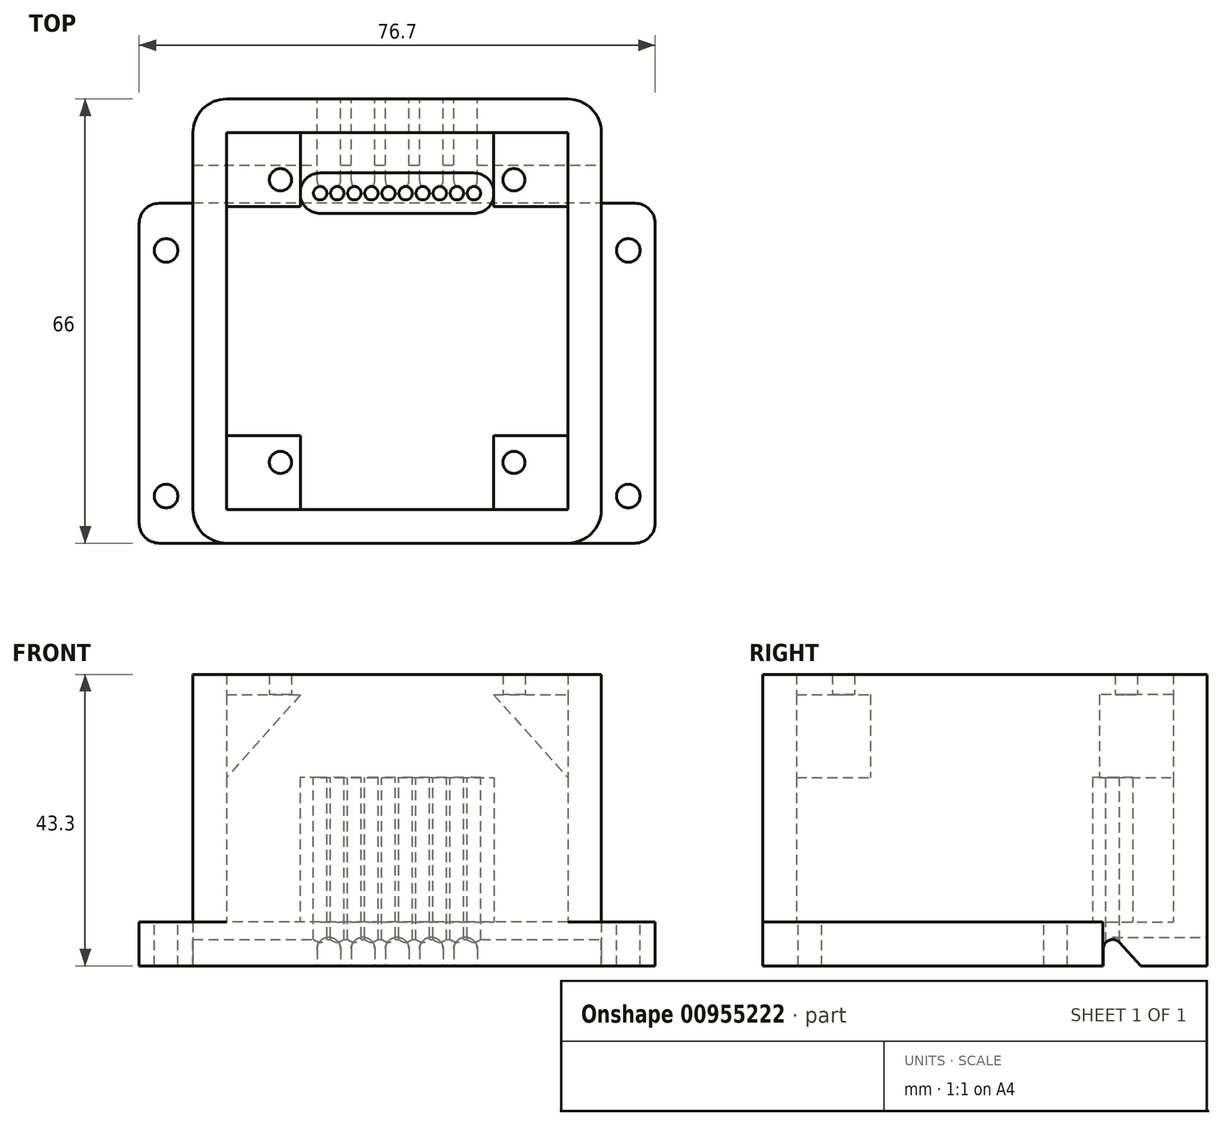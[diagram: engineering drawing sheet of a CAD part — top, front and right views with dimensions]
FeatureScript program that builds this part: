
annotation { "Feature Type Name" : "Feature", "Feature Type Description" : "" }
export const myFeature = defineFeature(function(context is Context, id is Id, definition is map)
    precondition{}
    {
        {
            var Q0;
            Q0=qCreatedBy(makeId("Top.planeOp"),FACE);
            var sketch = newSketch(context, id + "F0", { "sketchPlane" : qUnion([Q0])});
            skLineSegment(sketch, "E0.bottom", {"start": v(22.35, -25) * mm, "end": v(-22.35, -25) * mm});
            skLineSegment(sketch, "E0.top", {"start": v(22.35, 25) * mm, "end": v(-22.35, 25) * mm});
            skLineSegment(sketch, "E0.left", {"start": v(22.35, -25) * mm, "end": v(22.35, 25) * mm});
            skLineSegment(sketch, "E0.right", {"start": v(-22.35, -25) * mm, "end": v(-22.35, 25) * mm});
            skPoint(sketch, "E0.middle", {"position": v(0, 0) * mm});
            skSolve(sketch);
        }
        {
            var Q0;
            Q0=qCreatedBy(makeId("Top.planeOp"),FACE);
            var sketch = newSketch(context, id + "F1", { "sketchPlane" : qUnion([Q0])});
            skLineSegment(sketch, "E1.bottom", {"start": v(30.35, -33) * mm, "end": v(-30.35, -33) * mm});
            skLineSegment(sketch, "E1.top", {"start": v(25.35, 33) * mm, "end": v(-25.35, 33) * mm});
            skLineSegment(sketch, "E1.left", {"start": v(30.35, -33) * mm, "end": v(30.35, 28) * mm});
            skLineSegment(sketch, "E1.right", {"start": v(-30.35, -33) * mm, "end": v(-30.35, 28) * mm});
            skPoint(sketch, "E1.middle", {"position": v(0, 0) * mm});
            skPoint(sketch, "E2.visualSharp", {"position": v(-30.35, 33) * mm});
            skArc(sketch, "E2.filletArc", {"start": v(-25.35, 33) * mm, "mid": v(-28.89, 31.54) * mm, "end": v(-30.35, 28) * mm});
            skPoint(sketch, "E3.visualSharp", {"position": v(30.35, 33) * mm});
            skArc(sketch, "E3.filletArc", {"start": v(30.35, 28) * mm, "mid": v(28.89, 31.54) * mm, "end": v(25.35, 33) * mm});
            skPoint(sketch, "E4.visualSharp", {"position": v(-30.35, -33) * mm});
            skPoint(sketch, "E5.visualSharp", {"position": v(30.35, -33) * mm});
            skLineSegment(sketch, "E6", {"start": v(-20.48, 19) * mm, "end": v(20.95, 19) * mm, "construction": true});
            skLineSegment(sketch, "E7.bottom", {"start": v(-30.35, -33) * mm, "end": v(-35.35, -33) * mm});
            skLineSegment(sketch, "E7.top", {"start": v(-30.35, 17.5) * mm, "end": v(-35.35, 17.5) * mm});
            skLineSegment(sketch, "E7.left", {"start": v(-30.35, -33) * mm, "end": v(-30.35, 17.5) * mm});
            skLineSegment(sketch, "E7.right", {"start": v(-38.35, -30) * mm, "end": v(-38.35, 14.5) * mm});
            skPoint(sketch, "E8.oppositeSnap0", {"position": v(-34.35, 17.5) * mm});
            skLineSegment(sketch, "E8.bottom", {"start": v(30.35, -33) * mm, "end": v(35.35, -33) * mm});
            skLineSegment(sketch, "E8.top", {"start": v(30.35, 17.5) * mm, "end": v(35.35, 17.5) * mm});
            skLineSegment(sketch, "E8.left", {"start": v(30.35, -33) * mm, "end": v(30.35, 17.5) * mm});
            skLineSegment(sketch, "E8.right", {"start": v(38.35, -30) * mm, "end": v(38.35, 14.5) * mm});
            skPoint(sketch, "E9.visualSharp", {"position": v(-38.35, 17.5) * mm});
            skArc(sketch, "E9.filletArc", {"start": v(-35.35, 17.5) * mm, "mid": v(-37.47, 16.62) * mm, "end": v(-38.35, 14.5) * mm});
            skPoint(sketch, "E10.visualSharp", {"position": v(-38.35, -33) * mm});
            skArc(sketch, "E10.filletArc", {"start": v(-38.35, -30) * mm, "mid": v(-37.47, -32.12) * mm, "end": v(-35.35, -33) * mm});
            skPoint(sketch, "E11.visualSharp", {"position": v(38.35, 17.5) * mm});
            skArc(sketch, "E11.filletArc", {"start": v(38.35, 14.5) * mm, "mid": v(37.47, 16.62) * mm, "end": v(35.35, 17.5) * mm});
            skPoint(sketch, "E12.visualSharp", {"position": v(38.35, -33) * mm});
            skArc(sketch, "E12.filletArc", {"start": v(35.35, -33) * mm, "mid": v(37.47, -32.12) * mm, "end": v(38.35, -30) * mm});
            skSolve(sketch);
        }
        {
            var Q0;
            Q0=makeQuery(id+"F1.imprint","IMPRINT",FACE,{"disambiguationData":[TD([[makeQuery(id+"F1.imprint","IMPRINT",EDGE,{"derivedFrom":sQuery(id+"F1.wireOp",EDGE,"E1.bottom")}),-1.0]])]});
            var Q1;
            Q1=makeQuery(id+"F1.imprint","IMPRINT",FACE,{"disambiguationData":[TD([[makeQuery(id+"F1.imprint","IMPRINT",EDGE,{"derivedFrom":sQuery(id+"F1.wireOp",EDGE,"E7.bottom")}),-1.0]])]});
            var Q2;
            Q2=makeQuery(id+"F1.imprint","IMPRINT",FACE,{"disambiguationData":[TD([[makeQuery(id+"F1.imprint","IMPRINT",EDGE,{"derivedFrom":sQuery(id+"F1.wireOp",EDGE,"E8.bottom")}),1.0]])]});
            extrude(context, id + "F2", {"entities" : qUnion([Q0, Q1, Q2]), "depth" : 6.5 * mm, "offsetDistance" : 25 * mm});
        }
        {
            var Q0;
            Q0=makeQuery(id+"F2.opExtrude","CAP_FACE",FACE,{"disambiguationData":[OSD([sQuery(id+"F1.wireOp",EDGE,"E1.bottom"),sQuery(id+"F1.wireOp",EDGE,"E1.top"),sQuery(id+"F1.wireOp",EDGE,"E1.left"),sQuery(id+"F1.wireOp",EDGE,"E1.right"),sQuery(id+"F1.wireOp",EDGE,"E2.filletArc"),sQuery(id+"F1.wireOp",EDGE,"E3.filletArc"),sQuery(id+"F1.wireOp",EDGE,"E4.filletArc"),sQuery(id+"F1.wireOp",EDGE,"E5.filletArc")])],"isStart":false});
            var sketch = newSketch(context, id + "F3", { "sketchPlane" : qUnion([Q0])});
            skLineSegment(sketch, "E13.bottom", {"start": v(25.35, -28) * mm, "end": v(-25.35, -28) * mm});
            skLineSegment(sketch, "E13.top", {"start": v(25.35, 28) * mm, "end": v(-25.35, 28) * mm});
            skLineSegment(sketch, "E13.left", {"start": v(25.35, -28) * mm, "end": v(25.35, 28) * mm});
            skLineSegment(sketch, "E13.right", {"start": v(-25.35, -28) * mm, "end": v(-25.35, 28) * mm});
            skPoint(sketch, "E13.middle", {"position": v(0, 0) * mm});
            skLineSegment(sketch, "E14.bottom", {"start": v(-15.24, 28) * mm, "end": v(15.24, 28) * mm});
            skLineSegment(sketch, "E14.top", {"start": v(-11.45, 16) * mm, "end": v(11.4, 16) * mm});
            skPoint(sketch, "E15", {"position": v(-11.45, 19) * mm});
            skPoint(sketch, "E16", {"position": v(-8.91, 19) * mm});
            skPoint(sketch, "E17", {"position": v(-6.37, 19) * mm});
            skPoint(sketch, "E18", {"position": v(-3.83, 19) * mm});
            skPoint(sketch, "E19", {"position": v(-1.3, 19) * mm});
            skPoint(sketch, "E20", {"position": v(1.25, 19) * mm});
            skPoint(sketch, "E21", {"position": v(3.79, 19) * mm});
            skPoint(sketch, "E22", {"position": v(6.33, 19) * mm});
            skPoint(sketch, "E23", {"position": v(8.87, 19) * mm});
            skPoint(sketch, "E24", {"position": v(11.4, 19) * mm});
            skPoint(sketch, "E25.visualSharp", {"position": v(15.24, 16) * mm});
            skLineSegment(sketch, "E26.top", {"start": v(-11.45, 22) * mm, "end": v(11.4, 22) * mm});
            skArc(sketch, "E27", {"start": v(-11.45, 22) * mm, "mid": v(-14.45, 19) * mm, "end": v(-11.45, 16) * mm});
            skArc(sketch, "E28", {"start": v(11.4, 16) * mm, "mid": v(14.4, 19) * mm, "end": v(11.4, 22) * mm});
            skLineSegment(sketch, "E29.bottom", {"start": v(25.35, -33) * mm, "end": v(-25.35, -33) * mm});
            skLineSegment(sketch, "E29.top", {"start": v(25.35, 33) * mm, "end": v(-25.35, 33) * mm});
            skLineSegment(sketch, "E29.left", {"start": v(30.35, -28) * mm, "end": v(30.35, 28) * mm});
            skLineSegment(sketch, "E29.right", {"start": v(-30.35, -28) * mm, "end": v(-30.35, 28) * mm});
            skPoint(sketch, "E30.visualSharp", {"position": v(-30.35, -33) * mm});
            skArc(sketch, "E30.filletArc", {"start": v(-30.35, -28) * mm, "mid": v(-28.89, -31.54) * mm, "end": v(-25.35, -33) * mm});
            skPoint(sketch, "E31.visualSharp", {"position": v(30.35, -33) * mm});
            skArc(sketch, "E31.filletArc", {"start": v(25.35, -33) * mm, "mid": v(28.89, -31.54) * mm, "end": v(30.35, -28) * mm});
            skPoint(sketch, "E32.visualSharp", {"position": v(-30.35, 33) * mm});
            skArc(sketch, "E32.filletArc", {"start": v(-25.35, 33) * mm, "mid": v(-28.89, 31.54) * mm, "end": v(-30.35, 28) * mm});
            skPoint(sketch, "E33.visualSharp", {"position": v(30.35, 33) * mm});
            skArc(sketch, "E33.filletArc", {"start": v(30.35, 28) * mm, "mid": v(28.89, 31.54) * mm, "end": v(25.35, 33) * mm});
            skSolve(sketch);
        }
        {
            var Q0;
            Q0=makeQuery(id+"F3.imprint","IMPRINT",FACE,{"disambiguationData":[TD([[makeQuery(id+"F3.imprint","IMPRINT",EDGE,{"derivedFrom":sQuery(id+"F3.wireOp",EDGE,"E13.bottom")}),1.0]])]});
            var Q1;
            Q1=makeQuery(id+"F3.imprint","IMPRINT",FACE,{"disambiguationData":[TD([[makeQuery(id+"F3.imprint","IMPRINT",EDGE,{"derivedFrom":sQuery(id+"F3.wireOp",EDGE,"E14.top")}),1.0]])]});
            extrude(context, id + "F4", {"entities" : qUnion([Q0, Q1]), "operationType" : NewBodyOperationType.ADD, "depth" : 21.5 * mm, "offsetDistance" : 25 * mm});
        }
        {
            var Q0;
            {var subQ0=sQuery(id+"F1.wireOp",EDGE,"E1.left");Q0=makeQuery(id+"F4.boolean.opBoolean","MERGE",FACE,{"derivedFrom":[makeQuery(id+"F2.opExtrude","SWEPT_FACE",FACE,{"disambiguationData":[OSD([subQ0])]}),makeQuery(id+"F4.opExtrude","SWEPT_FACE",FACE,{"disambiguationData":[OSD([subQ0])]})]});}
            var sketch = newSketch(context, id + "F5", { "sketchPlane" : qUnion([Q0])});
            skLineSegment(sketch, "E34", {"start": v(19, 18.6) * mm, "end": v(19, -3.34) * mm, "construction": true});
            skPoint(sketch, "E35", {"position": v(19, 2.5) * mm});
            skCircle(sketch, "E36", {"center": v(19, 2.5) * mm, "radius": 1.4 * mm});
            skLineSegment(sketch, "E37", {"start": v(17.6, 2.5) * mm, "end": v(17.6, 0) * mm});
            skLineSegment(sketch, "E38", {"start": v(23.2, 0) * mm, "end": v(20.03, 3.45) * mm});
            skSolve(sketch);
        }
        {
            var Q0;
            {var subQ0=sQuery(id+"F5.wireOp",EDGE,"E36");var subQ1=makeQuery(id+"F5.imprint","INTERSECT",VERTEX,{"derivedFrom":[subQ0,sQuery(id+"F5.wireOp",EDGE,"E37")]});Q0=makeQuery(id+"F5.imprint","IMPRINT",FACE,{"disambiguationData":[TD([[makeQuery(id+"F5.imprint","IMPRINT",EDGE,{"disambiguationData":[TD([[subQ1,1.0]])],"derivedFrom":subQ0}),1.0]])]});}
            var Q1;
            {var subQ0=sQuery(id+"F5.wireOp",EDGE,"E37");Q1=makeQuery(id+"F5.imprint","IMPRINT",FACE,{"disambiguationData":[TD([[makeQuery(id+"F5.imprint","IMPRINT",EDGE,{"derivedFrom":subQ0}),1.0]])]});}
            extrude(context, id + "F6", {"entities" : qUnion([Q0, Q1]), "operationType" : NewBodyOperationType.REMOVE, "endBound" : BoundingType.THROUGH_ALL, "oppositeDirection" : true, "depth" : 25 * mm, "offsetDistance" : 25 * mm});
        }
        {
            var Q0;
            Q0=makeQuery(id+"F4.opExtrude","CAP_FACE",FACE,{"disambiguationData":[OSD([sQuery(id+"F3.wireOp",EDGE,"E13.bottom"),sQuery(id+"F3.wireOp",EDGE,"E13.top"),sQuery(id+"F3.wireOp",EDGE,"E13.left"),sQuery(id+"F3.wireOp",EDGE,"E13.right"),sQuery(id+"F3.wireOp",EDGE,"E29.bottom"),sQuery(id+"F3.wireOp",EDGE,"E29.top"),sQuery(id+"F3.wireOp",EDGE,"E29.left"),sQuery(id+"F3.wireOp",EDGE,"E29.right"),sQuery(id+"F3.wireOp",EDGE,"E30.filletArc"),sQuery(id+"F3.wireOp",EDGE,"E31.filletArc"),sQuery(id+"F3.wireOp",EDGE,"E32.filletArc"),sQuery(id+"F3.wireOp",EDGE,"E33.filletArc")])],"isStart":false});
            var sketch = newSketch(context, id + "F7", { "sketchPlane" : qUnion([Q0])});
            skPoint(sketch, "E39", {"position": v(-11.45, 19) * mm});
            skCircle(sketch, "E40", {"center": v(-11.45, 19) * mm, "radius": 1 * mm});
            skPoint(sketch, "E41", {"position": v(-8.91, 19) * mm});
            skPoint(sketch, "E42", {"position": v(-6.37, 19) * mm});
            skPoint(sketch, "E43", {"position": v(-3.83, 19) * mm});
            skPoint(sketch, "E44", {"position": v(-1.3, 19) * mm});
            skPoint(sketch, "E45", {"position": v(1.25, 19) * mm});
            skPoint(sketch, "E46", {"position": v(3.79, 19) * mm});
            skPoint(sketch, "E47", {"position": v(6.33, 19) * mm});
            skPoint(sketch, "E48", {"position": v(8.87, 19) * mm});
            skPoint(sketch, "E49", {"position": v(11.4, 19) * mm});
            skCircle(sketch, "E50", {"center": v(-8.91, 19) * mm, "radius": 1 * mm});
            skCircle(sketch, "E51", {"center": v(-6.37, 19) * mm, "radius": 1 * mm});
            skCircle(sketch, "E52", {"center": v(-3.83, 19) * mm, "radius": 1 * mm});
            skCircle(sketch, "E53", {"center": v(-1.3, 19) * mm, "radius": 1 * mm});
            skCircle(sketch, "E54", {"center": v(1.25, 19) * mm, "radius": 1 * mm});
            skCircle(sketch, "E55", {"center": v(3.79, 19) * mm, "radius": 1 * mm});
            skCircle(sketch, "E56", {"center": v(6.33, 19) * mm, "radius": 1 * mm});
            skCircle(sketch, "E57", {"center": v(8.87, 19) * mm, "radius": 1 * mm});
            skCircle(sketch, "E58", {"center": v(11.4, 19) * mm, "radius": 1 * mm});
            skSolve(sketch);
        }
        {
            var Q0;
            Q0=makeQuery(id+"F7.imprint","IMPRINT",FACE,{"disambiguationData":[TD([[makeQuery(id+"F7.imprint","IMPRINT",EDGE,{"derivedFrom":sQuery(id+"F7.wireOp",EDGE,"E53")}),1.0]])]});
            var Q1;
            Q1=makeQuery(id+"F7.imprint","IMPRINT",FACE,{"disambiguationData":[TD([[makeQuery(id+"F7.imprint","IMPRINT",EDGE,{"derivedFrom":sQuery(id+"F7.wireOp",EDGE,"E40")}),1.0]])]});
            var Q2;
            Q2=makeQuery(id+"F7.imprint","IMPRINT",FACE,{"disambiguationData":[TD([[makeQuery(id+"F7.imprint","IMPRINT",EDGE,{"derivedFrom":sQuery(id+"F7.wireOp",EDGE,"E50")}),1.0]])]});
            var Q3;
            Q3=makeQuery(id+"F7.imprint","IMPRINT",FACE,{"disambiguationData":[TD([[makeQuery(id+"F7.imprint","IMPRINT",EDGE,{"derivedFrom":sQuery(id+"F7.wireOp",EDGE,"E51")}),1.0]])]});
            var Q4;
            Q4=makeQuery(id+"F7.imprint","IMPRINT",FACE,{"disambiguationData":[TD([[makeQuery(id+"F7.imprint","IMPRINT",EDGE,{"derivedFrom":sQuery(id+"F7.wireOp",EDGE,"E52")}),1.0]])]});
            var Q5;
            Q5=makeQuery(id+"F7.imprint","IMPRINT",FACE,{"disambiguationData":[TD([[makeQuery(id+"F7.imprint","IMPRINT",EDGE,{"derivedFrom":sQuery(id+"F7.wireOp",EDGE,"E54")}),1.0]])]});
            var Q6;
            Q6=makeQuery(id+"F7.imprint","IMPRINT",FACE,{"disambiguationData":[TD([[makeQuery(id+"F7.imprint","IMPRINT",EDGE,{"derivedFrom":sQuery(id+"F7.wireOp",EDGE,"E55")}),1.0]])]});
            var Q7;
            Q7=makeQuery(id+"F7.imprint","IMPRINT",FACE,{"disambiguationData":[TD([[makeQuery(id+"F7.imprint","IMPRINT",EDGE,{"derivedFrom":sQuery(id+"F7.wireOp",EDGE,"E56")}),1.0]])]});
            var Q8;
            Q8=makeQuery(id+"F7.imprint","IMPRINT",FACE,{"disambiguationData":[TD([[makeQuery(id+"F7.imprint","IMPRINT",EDGE,{"derivedFrom":sQuery(id+"F7.wireOp",EDGE,"E57")}),1.0]])]});
            var Q9;
            Q9=makeQuery(id+"F7.imprint","IMPRINT",FACE,{"disambiguationData":[TD([[makeQuery(id+"F7.imprint","IMPRINT",EDGE,{"derivedFrom":sQuery(id+"F7.wireOp",EDGE,"E58")}),1.0]])]});
            extrude(context, id + "F8", {"entities" : qUnion([Q0, Q1, Q2, Q3, Q4, Q5, Q6, Q7, Q8, Q9]), "operationType" : NewBodyOperationType.REMOVE, "oppositeDirection" : true, "depth" : 26 * mm, "offsetDistance" : 25 * mm});
        }
        {
            var Q0;
            Q0=makeQuery(id+"F4.opExtrude","CAP_FACE",FACE,{"disambiguationData":[OSD([sQuery(id+"F3.wireOp",EDGE,"E13.bottom"),sQuery(id+"F3.wireOp",EDGE,"E13.top"),sQuery(id+"F3.wireOp",EDGE,"E13.left"),sQuery(id+"F3.wireOp",EDGE,"E13.right"),sQuery(id+"F3.wireOp",EDGE,"E29.bottom"),sQuery(id+"F3.wireOp",EDGE,"E29.top"),sQuery(id+"F3.wireOp",EDGE,"E29.left"),sQuery(id+"F3.wireOp",EDGE,"E29.right"),sQuery(id+"F3.wireOp",EDGE,"E30.filletArc"),sQuery(id+"F3.wireOp",EDGE,"E31.filletArc"),sQuery(id+"F3.wireOp",EDGE,"E32.filletArc"),sQuery(id+"F3.wireOp",EDGE,"E33.filletArc")])],"isStart":false});
            var sketch = newSketch(context, id + "F9", { "sketchPlane" : qUnion([Q0])});
            skLineSegment(sketch, "E59.bottom", {"start": v(-25.35, 28) * mm, "end": v(-14.35, 28) * mm});
            skLineSegment(sketch, "E59.top", {"start": v(-25.35, 17) * mm, "end": v(-14.35, 17) * mm});
            skLineSegment(sketch, "E59.left", {"start": v(-25.35, 28) * mm, "end": v(-25.35, 17) * mm});
            skLineSegment(sketch, "E59.right", {"start": v(-14.35, 28) * mm, "end": v(-14.35, 17) * mm});
            skLineSegment(sketch, "E60.bottom", {"start": v(25.35, 28) * mm, "end": v(14.35, 28) * mm});
            skLineSegment(sketch, "E60.top", {"start": v(25.35, 17) * mm, "end": v(14.35, 17) * mm});
            skLineSegment(sketch, "E60.left", {"start": v(25.35, 28) * mm, "end": v(25.35, 17) * mm});
            skLineSegment(sketch, "E60.right", {"start": v(14.35, 28) * mm, "end": v(14.35, 17) * mm});
            skLineSegment(sketch, "E61.bottom", {"start": v(-25.35, -28) * mm, "end": v(-14.35, -28) * mm});
            skLineSegment(sketch, "E61.top", {"start": v(-25.35, -17) * mm, "end": v(-14.35, -17) * mm});
            skLineSegment(sketch, "E61.left", {"start": v(-25.35, -28) * mm, "end": v(-25.35, -17) * mm});
            skLineSegment(sketch, "E61.right", {"start": v(-14.35, -28) * mm, "end": v(-14.35, -17) * mm});
            skLineSegment(sketch, "E62.bottom", {"start": v(25.35, -28) * mm, "end": v(14.35, -28) * mm});
            skLineSegment(sketch, "E62.top", {"start": v(25.35, -17) * mm, "end": v(14.35, -17) * mm});
            skLineSegment(sketch, "E62.left", {"start": v(25.35, -28) * mm, "end": v(25.35, -17) * mm});
            skLineSegment(sketch, "E62.right", {"start": v(14.35, -28) * mm, "end": v(14.35, -17) * mm});
            skSolve(sketch);
        }
        {
            var Q0;
            {var subQ5=sQuery(id+"F9.wireOp",EDGE,"E59.bottom");Q0=makeQuery(id+"F9.imprint","IMPRINT",FACE,{"disambiguationData":[TD([[makeQuery(id+"F9.imprint","IMPRINT",EDGE,{"derivedFrom":subQ5}),-1.0]])]});}
            var Q1;
            Q1=makeQuery(id+"F9.imprint","IMPRINT",FACE,{"disambiguationData":[TD([[makeQuery(id+"F9.imprint","IMPRINT",EDGE,{"derivedFrom":sQuery(id+"F9.wireOp",EDGE,"E59.bottom")}),1.0]])]});
            var Q2;
            Q2=makeQuery(id+"F9.imprint","IMPRINT",FACE,{"disambiguationData":[TD([[makeQuery(id+"F9.imprint","IMPRINT",EDGE,{"derivedFrom":sQuery(id+"F9.wireOp",EDGE,"E60.bottom")}),1.0]])]});
            var Q3;
            Q3=makeQuery(id+"F9.imprint","IMPRINT",FACE,{"disambiguationData":[TD([[makeQuery(id+"F9.imprint","IMPRINT",EDGE,{"derivedFrom":sQuery(id+"F9.wireOp",EDGE,"E61.bottom")}),-1.0]])]});
            var Q4;
            Q4=makeQuery(id+"F9.imprint","IMPRINT",FACE,{"disambiguationData":[TD([[makeQuery(id+"F9.imprint","IMPRINT",EDGE,{"derivedFrom":sQuery(id+"F9.wireOp",EDGE,"E62.bottom")}),-1.0]])]});
            extrude(context, id + "F10", {"entities" : qUnion([Q0, Q1, Q2, Q3, Q4]), "operationType" : NewBodyOperationType.ADD, "depth" : 12.3 * mm, "offsetDistance" : 25 * mm});
        }
        {
            var Q0;
            Q0=makeQuery(id+"F10.opExtrude","SWEPT_FACE",FACE,{"disambiguationData":[OSD([sQuery(id+"F9.wireOp",EDGE,"E59.top")])]});
            var sketch = newSketch(context, id + "F11", { "sketchPlane" : qUnion([Q0])});
            skLineSegment(sketch, "E63", {"start": v(-14.35, 40.3) * mm, "end": v(-25.35, 28) * mm});
            skLineSegment(sketch, "E64", {"start": v(-25.35, 28) * mm, "end": v(-14.35, 28) * mm});
            skLineSegment(sketch, "E65", {"start": v(-14.35, 28) * mm, "end": v(-14.35, 40.3) * mm});
            skSolve(sketch);
        }
        {
            var Q0;
            {var subQ0=sQuery(id+"F11.wireOp",EDGE,"E63");Q0=makeQuery(id+"F11.imprint","IMPRINT",FACE,{"disambiguationData":[TD([[makeQuery(id+"F11.imprint","IMPRINT",EDGE,{"derivedFrom":subQ0}),1.0]])]});}
            extrude(context, id + "F12", {"entities" : qUnion([Q0]), "operationType" : NewBodyOperationType.REMOVE, "oppositeDirection" : true, "depth" : 11 * mm, "offsetDistance" : 25 * mm});
        }
        {
            var Q0;
            Q0=makeQuery(id+"F10.opExtrude","SWEPT_FACE",FACE,{"disambiguationData":[OSD([sQuery(id+"F9.wireOp",EDGE,"E60.top")])]});
            var sketch = newSketch(context, id + "F13", { "sketchPlane" : qUnion([Q0])});
            skLineSegment(sketch, "E66", {"start": v(14.35, 40.3) * mm, "end": v(25.35, 28) * mm});
            skLineSegment(sketch, "E67", {"start": v(25.35, 28) * mm, "end": v(14.35, 28) * mm});
            skLineSegment(sketch, "E68", {"start": v(14.35, 28) * mm, "end": v(14.35, 40.3) * mm});
            skSolve(sketch);
        }
        {
            var Q0;
            {var subQ0=sQuery(id+"F13.wireOp",EDGE,"E66");Q0=makeQuery(id+"F13.imprint","IMPRINT",FACE,{"disambiguationData":[TD([[makeQuery(id+"F13.imprint","IMPRINT",EDGE,{"derivedFrom":subQ0}),-1.0]])]});}
            extrude(context, id + "F14", {"entities" : qUnion([Q0]), "operationType" : NewBodyOperationType.REMOVE, "oppositeDirection" : true, "depth" : 11 * mm, "offsetDistance" : 25 * mm});
        }
        {
            var Q0;
            Q0=makeQuery(id+"F10.opExtrude","SWEPT_FACE",FACE,{"disambiguationData":[OSD([sQuery(id+"F9.wireOp",EDGE,"E62.top")])]});
            var sketch = newSketch(context, id + "F15", { "sketchPlane" : qUnion([Q0])});
            skLineSegment(sketch, "E69", {"start": v(-25.35, 28) * mm, "end": v(-14.35, 40.3) * mm});
            skLineSegment(sketch, "E70", {"start": v(-14.35, 40.3) * mm, "end": v(-14.35, 28) * mm});
            skLineSegment(sketch, "E71", {"start": v(-14.35, 28) * mm, "end": v(-25.35, 28) * mm});
            skSolve(sketch);
        }
        {
            var Q0;
            Q0=makeQuery(id+"F15.imprint","IMPRINT",FACE,{"disambiguationData":[TD([[makeQuery(id+"F15.imprint","IMPRINT",EDGE,{"derivedFrom":sQuery(id+"F15.wireOp",EDGE,"E69")}),-1.0]])]});
            extrude(context, id + "F16", {"entities" : qUnion([Q0]), "operationType" : NewBodyOperationType.REMOVE, "oppositeDirection" : true, "depth" : 11 * mm, "offsetDistance" : 25 * mm});
        }
        {
            var Q0;
            Q0=makeQuery(id+"F10.opExtrude","SWEPT_FACE",FACE,{"disambiguationData":[OSD([sQuery(id+"F9.wireOp",EDGE,"E61.top")])]});
            var sketch = newSketch(context, id + "F17", { "sketchPlane" : qUnion([Q0])});
            skLineSegment(sketch, "E72", {"start": v(14.35, 40.3) * mm, "end": v(25.35, 28) * mm});
            skLineSegment(sketch, "E73", {"start": v(25.35, 28) * mm, "end": v(14.35, 28) * mm});
            skLineSegment(sketch, "E74", {"start": v(14.35, 28) * mm, "end": v(14.35, 40.3) * mm});
            skSolve(sketch);
        }
        {
            var Q0;
            Q0=makeQuery(id+"F17.imprint","IMPRINT",FACE,{"disambiguationData":[TD([[makeQuery(id+"F17.imprint","IMPRINT",EDGE,{"derivedFrom":sQuery(id+"F17.wireOp",EDGE,"E72")}),-1.0]])]});
            extrude(context, id + "F18", {"entities" : qUnion([Q0]), "operationType" : NewBodyOperationType.REMOVE, "oppositeDirection" : true, "depth" : 11 * mm, "offsetDistance" : 25 * mm});
        }
        {
            var Q0;
            Q0=makeQuery(id+"F10.opExtrude","CAP_FACE",FACE,{"disambiguationData":[OSD([sQuery(id+"F3.wireOp",EDGE,"E13.bottom"),sQuery(id+"F3.wireOp",EDGE,"E13.top"),sQuery(id+"F3.wireOp",EDGE,"E13.left"),sQuery(id+"F3.wireOp",EDGE,"E13.right"),sQuery(id+"F3.wireOp",EDGE,"E29.bottom"),sQuery(id+"F3.wireOp",EDGE,"E29.top"),sQuery(id+"F3.wireOp",EDGE,"E29.left"),sQuery(id+"F3.wireOp",EDGE,"E29.right"),sQuery(id+"F3.wireOp",EDGE,"E30.filletArc"),sQuery(id+"F3.wireOp",EDGE,"E31.filletArc"),sQuery(id+"F3.wireOp",EDGE,"E32.filletArc"),sQuery(id+"F3.wireOp",EDGE,"E33.filletArc"),sQuery(id+"F9.wireOp",EDGE,"E59.top"),sQuery(id+"F9.wireOp",EDGE,"E59.right"),sQuery(id+"F9.wireOp",EDGE,"E60.top"),sQuery(id+"F9.wireOp",EDGE,"E60.right"),sQuery(id+"F9.wireOp",EDGE,"E61.top"),sQuery(id+"F9.wireOp",EDGE,"E61.right"),sQuery(id+"F9.wireOp",EDGE,"E62.top"),sQuery(id+"F9.wireOp",EDGE,"E62.right")])],"isStart":false});
            var sketch = newSketch(context, id + "F19", { "sketchPlane" : qUnion([Q0])});
            skPoint(sketch, "E75", {"position": v(-17.35, 21) * mm});
            skPoint(sketch, "E76", {"position": v(17.35, 21) * mm});
            skCircle(sketch, "E77", {"center": v(-17.35, 21) * mm, "radius": 1.65 * mm});
            skCircle(sketch, "E78", {"center": v(17.35, 21) * mm, "radius": 1.65 * mm});
            skLineSegment(sketch, "E79.bottom", {"start": v(-25.35, 28) * mm, "end": v(25.35, 28) * mm});
            skLineSegment(sketch, "E79.top", {"start": v(-25.35, -28) * mm, "end": v(25.35, -28) * mm});
            skLineSegment(sketch, "E79.left", {"start": v(-25.35, 28) * mm, "end": v(-25.35, -28) * mm});
            skLineSegment(sketch, "E79.right", {"start": v(25.35, 28) * mm, "end": v(25.35, -28) * mm});
            skPoint(sketch, "E80", {"position": v(-17.35, -21) * mm});
            skPoint(sketch, "E81", {"position": v(17.35, -21) * mm});
            skCircle(sketch, "E82", {"center": v(-17.35, -21) * mm, "radius": 1.65 * mm});
            skCircle(sketch, "E83", {"center": v(17.35, -21) * mm, "radius": 1.65 * mm});
            skSolve(sketch);
        }
        {
            var Q0;
            Q0=makeQuery(id+"F19.imprint","IMPRINT",FACE,{"disambiguationData":[TD([[makeQuery(id+"F19.imprint","IMPRINT",EDGE,{"derivedFrom":makeQuery(id+"F10.opExtrude","CAP_EDGE",EDGE,{"disambiguationData":[OSD([sQuery(id+"F1.wireOp",EDGE,"E1.bottom")])],"isStart":false})}),-1.0]])]});
            var Q1;
            Q1=makeQuery(id+"F19.imprint","IMPRINT",FACE,{"disambiguationData":[TD([[makeQuery(id+"F19.imprint","IMPRINT",EDGE,{"derivedFrom":sQuery(id+"F19.wireOp",EDGE,"E77")}),1.0]])]});
            var Q2;
            Q2=makeQuery(id+"F19.imprint","IMPRINT",FACE,{"disambiguationData":[TD([[makeQuery(id+"F19.imprint","IMPRINT",EDGE,{"derivedFrom":sQuery(id+"F19.wireOp",EDGE,"E78")}),1.0]])]});
            var Q3;
            Q3=makeQuery(id+"F19.imprint","IMPRINT",FACE,{"disambiguationData":[TD([[makeQuery(id+"F19.imprint","IMPRINT",EDGE,{"derivedFrom":sQuery(id+"F19.wireOp",EDGE,"E82")}),1.0]])]});
            var Q4;
            Q4=makeQuery(id+"F19.imprint","IMPRINT",FACE,{"disambiguationData":[TD([[makeQuery(id+"F19.imprint","IMPRINT",EDGE,{"derivedFrom":sQuery(id+"F19.wireOp",EDGE,"E83")}),1.0]])]});
            var Q5;
            Q5=makeQuery(id+"F19.imprint","IMPRINT",FACE,{"disambiguationData":[TD([[makeQuery(id+"F19.imprint","IMPRINT",EDGE,{"derivedFrom":makeQuery(id+"F10.opExtrude","CAP_EDGE",EDGE,{"disambiguationData":[OSD([sQuery(id+"F3.wireOp",EDGE,"E29.bottom")])],"isStart":false})}),-1.0]])]});
            extrude(context, id + "F20", {"entities" : qUnion([Q0, Q1, Q2, Q3, Q4, Q5]), "operationType" : NewBodyOperationType.ADD, "depth" : 3 * mm, "offsetDistance" : 25 * mm});
        }
        {
            var Q0;
            {var subQ0=sQuery(id+"F1.wireOp",EDGE,"E7.right");var subQ1=sQuery(id+"F1.wireOp",EDGE,"E7.top");var subQ2=sQuery(id+"F1.wireOp",EDGE,"E1.right");var subQ3=sQuery(id+"F1.wireOp",EDGE,"E8.bottom");var subQ4=sQuery(id+"F1.wireOp",EDGE,"E7.bottom");var subQ5=sQuery(id+"F1.wireOp",EDGE,"E1.bottom");var subQ6=sQuery(id+"F1.wireOp",EDGE,"E10.filletArc");var subQ7=sQuery(id+"F1.wireOp",EDGE,"E9.filletArc");Q0=makeQuery(id+"F4.boolean.opBoolean","SPLIT",FACE,{"disambiguationData":[TD([makeQuery(id+"F2.opExtrude","SWEPT_FACE",FACE,{"disambiguationData":[OSD([subQ2])]})])],"derivedFrom":makeQuery(id+"F2.opExtrude","CAP_FACE",FACE,{"disambiguationData":[OSD([subQ5,sQuery(id+"F1.wireOp",EDGE,"E1.top"),sQuery(id+"F1.wireOp",EDGE,"E1.left"),subQ2,sQuery(id+"F1.wireOp",EDGE,"E2.filletArc"),sQuery(id+"F1.wireOp",EDGE,"E3.filletArc"),subQ4,subQ1,subQ0,subQ3,sQuery(id+"F1.wireOp",EDGE,"E8.top"),sQuery(id+"F1.wireOp",EDGE,"E8.right"),subQ7,subQ6,sQuery(id+"F1.wireOp",EDGE,"E11.filletArc"),sQuery(id+"F1.wireOp",EDGE,"E12.filletArc")])],"isStart":false})});}
            var sketch = newSketch(context, id + "F21", { "sketchPlane" : qUnion([Q0])});
            skPoint(sketch, "E84", {"position": v(-34.35, 10.5) * mm});
            skPoint(sketch, "E85", {"position": v(34.35, 10.5) * mm});
            skPoint(sketch, "E86", {"position": v(34.35, -26) * mm});
            skPoint(sketch, "E87", {"position": v(-34.35, -26) * mm});
            skCircle(sketch, "E88", {"center": v(-34.35, 10.5) * mm, "radius": 1.75 * mm});
            skCircle(sketch, "E89", {"center": v(34.35, 10.5) * mm, "radius": 1.75 * mm});
            skCircle(sketch, "E90", {"center": v(-34.35, -26) * mm, "radius": 1.75 * mm});
            skCircle(sketch, "E91", {"center": v(34.35, -26) * mm, "radius": 1.75 * mm});
            skSolve(sketch);
        }
        {
            var Q0;
            Q0=makeQuery(id+"F21.imprint","IMPRINT",FACE,{"disambiguationData":[TD([[makeQuery(id+"F21.imprint","IMPRINT",EDGE,{"derivedFrom":sQuery(id+"F21.wireOp",EDGE,"E88")}),1.0]])]});
            var Q1;
            Q1=makeQuery(id+"F21.imprint","IMPRINT",FACE,{"disambiguationData":[TD([[makeQuery(id+"F21.imprint","IMPRINT",EDGE,{"derivedFrom":sQuery(id+"F21.wireOp",EDGE,"E90")}),1.0]])]});
            var Q2;
            Q2=makeQuery(id+"F21.imprint","IMPRINT",FACE,{"disambiguationData":[TD([[makeQuery(id+"F21.imprint","IMPRINT",EDGE,{"derivedFrom":sQuery(id+"F21.wireOp",EDGE,"E89")}),1.0]])]});
            var Q3;
            Q3=makeQuery(id+"F21.imprint","IMPRINT",FACE,{"disambiguationData":[TD([[makeQuery(id+"F21.imprint","IMPRINT",EDGE,{"derivedFrom":sQuery(id+"F21.wireOp",EDGE,"E91")}),1.0]])]});
            extrude(context, id + "F22", {"entities" : qUnion([Q0, Q1, Q2, Q3]), "operationType" : NewBodyOperationType.REMOVE, "endBound" : BoundingType.THROUGH_ALL, "oppositeDirection" : true, "depth" : 25 * mm, "offsetDistance" : 25 * mm});
        }
        {
            var Q0;
            {var subQ0=sQuery(id+"F3.wireOp",EDGE,"E29.top");Q0=makeQuery(id+"F20.boolean.opBoolean","MERGE",FACE,{"derivedFrom":[makeQuery(id+"F10.boolean.opBoolean","MERGE",FACE,{"derivedFrom":[makeQuery(id+"F4.boolean.opBoolean","MERGE",FACE,{"derivedFrom":[makeQuery(id+"F2.opExtrude","SWEPT_FACE",FACE,{"disambiguationData":[OSD([sQuery(id+"F1.wireOp",EDGE,"E1.top")])]}),makeQuery(id+"F4.opExtrude","SWEPT_FACE",FACE,{"disambiguationData":[OSD([subQ0])]})]}),makeQuery(id+"F10.opExtrude","SWEPT_FACE",FACE,{"disambiguationData":[OSD([subQ0])]})]}),makeQuery(id+"F20.opExtrude","SWEPT_FACE",FACE,{"disambiguationData":[OSD([subQ0])]})]});}
            var sketch = newSketch(context, id + "F23", { "sketchPlane" : qUnion([Q0])});
            skLineSegment(sketch, "E92", {"start": v(0, 0.67) * mm, "end": v(0, 43.3) * mm, "construction": true});
            skPoint(sketch, "E93", {"position": v(0, 2.5) * mm});
            skPoint(sketch, "E94", {"position": v(5.08, 2.5) * mm});
            skPoint(sketch, "E95", {"position": v(10.16, 2.5) * mm});
            skPoint(sketch, "E96", {"position": v(-5.08, 2.5) * mm});
            skPoint(sketch, "E97", {"position": v(-10.16, 2.5) * mm});
            skCircle(sketch, "E98", {"center": v(-10.16, 2.5) * mm, "radius": 1.75 * mm});
            skCircle(sketch, "E99", {"center": v(-5.08, 2.5) * mm, "radius": 1.75 * mm});
            skCircle(sketch, "E100", {"center": v(0, 2.5) * mm, "radius": 1.75 * mm});
            skCircle(sketch, "E101", {"center": v(5.08, 2.5) * mm, "radius": 1.75 * mm});
            skCircle(sketch, "E102", {"center": v(10.16, 2.5) * mm, "radius": 1.75 * mm});
            skLineSegment(sketch, "E103", {"start": v(-11.9, 2.5) * mm, "end": v(-11.9, 0) * mm});
            skLineSegment(sketch, "E104", {"start": v(-8.4, 2.5) * mm, "end": v(-8.4, 0) * mm});
            skLineSegment(sketch, "E105", {"start": v(-6.83, 2.5) * mm, "end": v(-6.83, 0) * mm});
            skLineSegment(sketch, "E106", {"start": v(-3.33, 2.5) * mm, "end": v(-3.33, 0) * mm});
            skLineSegment(sketch, "E107", {"start": v(-1.75, 2.5) * mm, "end": v(-1.75, 0) * mm});
            skLineSegment(sketch, "E108", {"start": v(1.75, 2.5) * mm, "end": v(1.75, 0) * mm});
            skLineSegment(sketch, "E109", {"start": v(6.83, 2.5) * mm, "end": v(6.83, 0) * mm});
            skLineSegment(sketch, "E110", {"start": v(3.33, 2.5) * mm, "end": v(3.33, 0) * mm});
            skLineSegment(sketch, "E111", {"start": v(8.4, 2.5) * mm, "end": v(8.4, 0) * mm});
            skLineSegment(sketch, "E112", {"start": v(11.9, 2.5) * mm, "end": v(11.9, 0) * mm});
            skSolve(sketch);
        }
        {
            var Q0;
            {var subQ0=sQuery(id+"F23.wireOp",EDGE,"E98");var subQ1=makeQuery(id+"F23.imprint","INTERSECT",VERTEX,{"derivedFrom":[subQ0,sQuery(id+"F23.wireOp",EDGE,"E103")]});Q0=makeQuery(id+"F23.imprint","IMPRINT",FACE,{"disambiguationData":[TD([[makeQuery(id+"F23.imprint","IMPRINT",EDGE,{"disambiguationData":[TD([[subQ1,1.0]])],"derivedFrom":subQ0}),1.0]])]});}
            var Q1;
            {var subQ0=sQuery(id+"F23.wireOp",EDGE,"E103");Q1=makeQuery(id+"F23.imprint","IMPRINT",FACE,{"disambiguationData":[TD([[makeQuery(id+"F23.imprint","IMPRINT",EDGE,{"derivedFrom":subQ0}),1.0]])]});}
            var Q2;
            {var subQ0=sQuery(id+"F23.wireOp",EDGE,"E99");var subQ1=makeQuery(id+"F23.imprint","INTERSECT",VERTEX,{"derivedFrom":[subQ0,sQuery(id+"F23.wireOp",EDGE,"E105")]});Q2=makeQuery(id+"F23.imprint","IMPRINT",FACE,{"disambiguationData":[TD([[makeQuery(id+"F23.imprint","IMPRINT",EDGE,{"disambiguationData":[TD([[subQ1,1.0]])],"derivedFrom":subQ0}),1.0]])]});}
            var Q3;
            {var subQ0=sQuery(id+"F23.wireOp",EDGE,"E105");Q3=makeQuery(id+"F23.imprint","IMPRINT",FACE,{"disambiguationData":[TD([[makeQuery(id+"F23.imprint","IMPRINT",EDGE,{"derivedFrom":subQ0}),1.0]])]});}
            var Q4;
            {var subQ0=sQuery(id+"F23.wireOp",EDGE,"E100");var subQ1=makeQuery(id+"F23.imprint","INTERSECT",VERTEX,{"derivedFrom":[subQ0,sQuery(id+"F23.wireOp",EDGE,"E107")]});Q4=makeQuery(id+"F23.imprint","IMPRINT",FACE,{"disambiguationData":[TD([[makeQuery(id+"F23.imprint","IMPRINT",EDGE,{"disambiguationData":[TD([[subQ1,1.0]])],"derivedFrom":subQ0}),1.0]])]});}
            var Q5;
            {var subQ0=sQuery(id+"F23.wireOp",EDGE,"E107");Q5=makeQuery(id+"F23.imprint","IMPRINT",FACE,{"disambiguationData":[TD([[makeQuery(id+"F23.imprint","IMPRINT",EDGE,{"derivedFrom":subQ0}),1.0]])]});}
            var Q6;
            {var subQ0=sQuery(id+"F23.wireOp",EDGE,"E101");var subQ1=makeQuery(id+"F23.imprint","INTERSECT",VERTEX,{"derivedFrom":[subQ0,sQuery(id+"F23.wireOp",EDGE,"E109")]});Q6=makeQuery(id+"F23.imprint","IMPRINT",FACE,{"disambiguationData":[TD([[makeQuery(id+"F23.imprint","IMPRINT",EDGE,{"disambiguationData":[TD([[subQ1,-1.0]])],"derivedFrom":subQ0}),1.0]])]});}
            var Q7;
            {var subQ0=sQuery(id+"F23.wireOp",EDGE,"E109");Q7=makeQuery(id+"F23.imprint","IMPRINT",FACE,{"disambiguationData":[TD([[makeQuery(id+"F23.imprint","IMPRINT",EDGE,{"derivedFrom":subQ0}),-1.0]])]});}
            var Q8;
            {var subQ0=sQuery(id+"F23.wireOp",EDGE,"E102");var subQ1=makeQuery(id+"F23.imprint","INTERSECT",VERTEX,{"derivedFrom":[subQ0,sQuery(id+"F23.wireOp",EDGE,"E111")]});Q8=makeQuery(id+"F23.imprint","IMPRINT",FACE,{"disambiguationData":[TD([[makeQuery(id+"F23.imprint","IMPRINT",EDGE,{"disambiguationData":[TD([[subQ1,1.0]])],"derivedFrom":subQ0}),1.0]])]});}
            var Q9;
            {var subQ0=sQuery(id+"F23.wireOp",EDGE,"E111");Q9=makeQuery(id+"F23.imprint","IMPRINT",FACE,{"disambiguationData":[TD([[makeQuery(id+"F23.imprint","IMPRINT",EDGE,{"derivedFrom":subQ0}),1.0]])]});}
            extrude(context, id + "F24", {"entities" : qUnion([Q0, Q1, Q2, Q3, Q4, Q5, Q6, Q7, Q8, Q9]), "operationType" : NewBodyOperationType.REMOVE, "oppositeDirection" : true, "depth" : 14 * mm, "offsetDistance" : 25 * mm});
        }
    });
